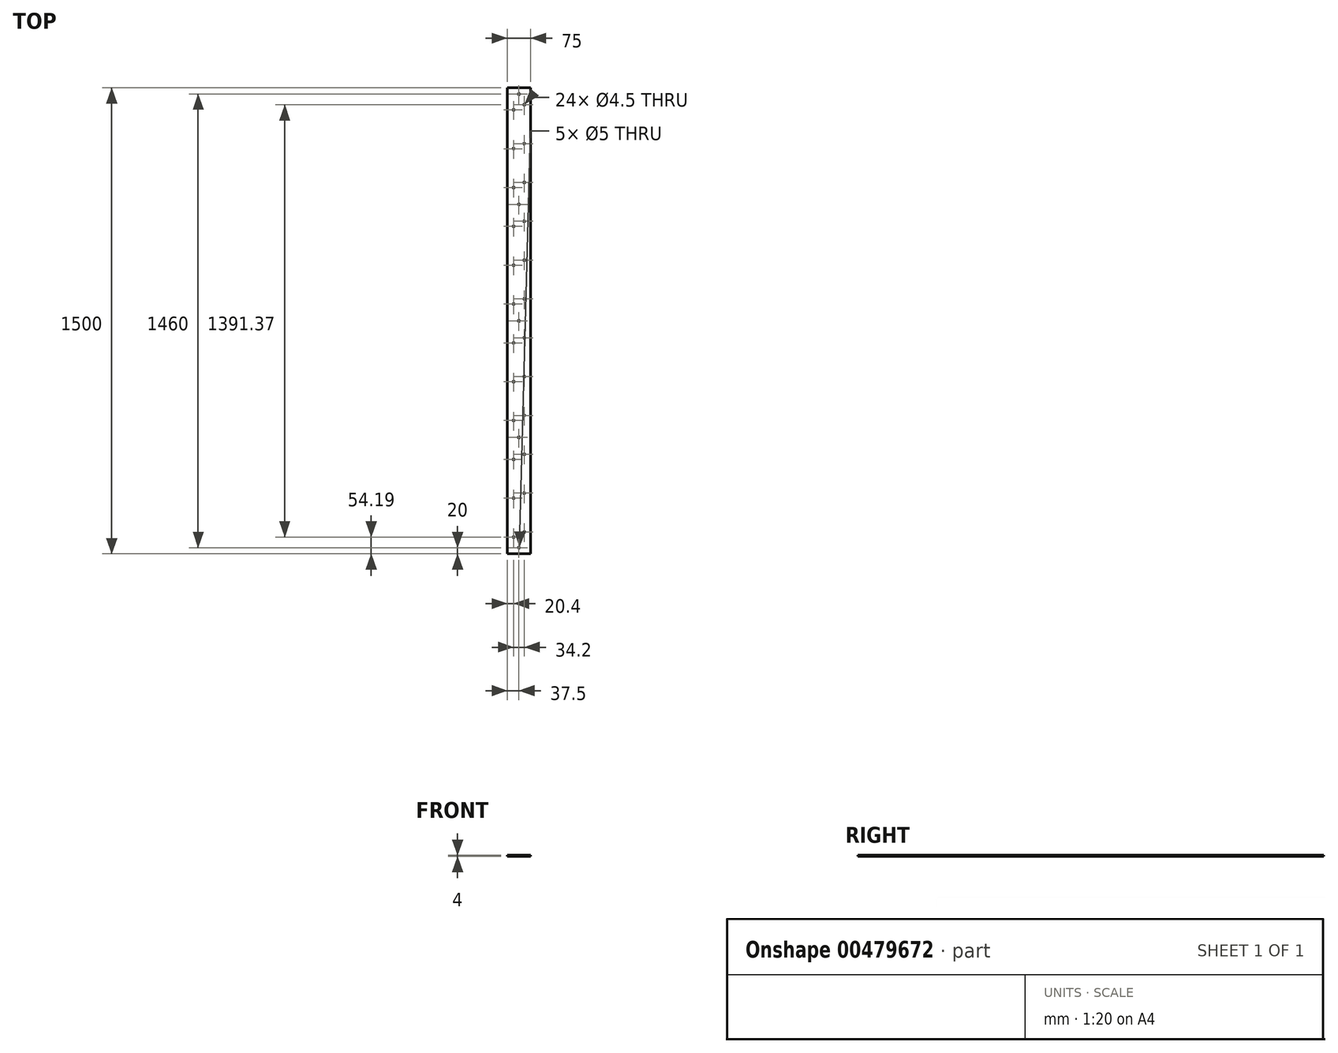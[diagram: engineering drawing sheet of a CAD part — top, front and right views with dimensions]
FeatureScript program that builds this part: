
annotation { "Feature Type Name" : "Feature", "Feature Type Description" : "" }
export const myFeature = defineFeature(function(context is Context, id is Id, definition is map)
    precondition{}
    {
        {
            var Q0;
            Q0=qCreatedBy(makeId("Top.planeOp"),FACE);
            var sketch = newSketch(context, id + "F0", { "sketchPlane" : qUnion([Q0])});
            skLineSegment(sketch, "E0.bottom", {"start": v(37.5, -750) * mm, "end": v(-37.5, -750) * mm});
            skLineSegment(sketch, "E0.top", {"start": v(37.5, 750) * mm, "end": v(-37.5, 750) * mm});
            skLineSegment(sketch, "E0.left", {"start": v(37.5, -750) * mm, "end": v(37.5, 750) * mm});
            skLineSegment(sketch, "E0.right", {"start": v(-37.5, -750) * mm, "end": v(-37.5, 750) * mm});
            skPoint(sketch, "E0.middle", {"position": v(0, 0) * mm});
            skCircle(sketch, "E1", {"center": v(-17.1, -695.81) * mm, "radius": 2.25 * mm});
            skCircle(sketch, "E2", {"center": v(17.1, -679.44) * mm, "radius": 2.25 * mm});
            skCircle(sketch, "E3.0.1.0", {"center": v(-17.1, -570.81) * mm, "radius": 2.25 * mm});
            skCircle(sketch, "E3.0.1.1", {"center": v(17.1, -554.44) * mm, "radius": 2.25 * mm});
            skCircle(sketch, "E3.0.2.0", {"center": v(-17.1, -445.81) * mm, "radius": 2.25 * mm});
            skCircle(sketch, "E3.0.2.1", {"center": v(17.1, -429.44) * mm, "radius": 2.25 * mm});
            skCircle(sketch, "E3.0.3.0", {"center": v(-17.1, -320.81) * mm, "radius": 2.25 * mm});
            skCircle(sketch, "E3.0.3.1", {"center": v(17.1, -304.44) * mm, "radius": 2.25 * mm});
            skCircle(sketch, "E3.0.4.0", {"center": v(-17.1, -195.81) * mm, "radius": 2.25 * mm});
            skCircle(sketch, "E3.0.4.1", {"center": v(17.1, -179.44) * mm, "radius": 2.25 * mm});
            skCircle(sketch, "E3.0.5.0", {"center": v(-17.1, -70.81) * mm, "radius": 2.25 * mm});
            skCircle(sketch, "E3.0.5.1", {"center": v(17.1, -54.44) * mm, "radius": 2.25 * mm});
            skCircle(sketch, "E3.0.6.0", {"center": v(-17.1, 54.19) * mm, "radius": 2.25 * mm});
            skCircle(sketch, "E3.0.6.1", {"center": v(17.1, 70.56) * mm, "radius": 2.25 * mm});
            skCircle(sketch, "E3.0.7.0", {"center": v(-17.1, 179.19) * mm, "radius": 2.25 * mm});
            skCircle(sketch, "E3.0.7.1", {"center": v(17.1, 195.56) * mm, "radius": 2.25 * mm});
            skCircle(sketch, "E3.0.8.0", {"center": v(-17.1, 304.19) * mm, "radius": 2.25 * mm});
            skCircle(sketch, "E3.0.8.1", {"center": v(17.1, 320.56) * mm, "radius": 2.25 * mm});
            skCircle(sketch, "E3.0.9.0", {"center": v(-17.1, 429.19) * mm, "radius": 2.25 * mm});
            skCircle(sketch, "E3.0.9.1", {"center": v(17.1, 445.56) * mm, "radius": 2.25 * mm});
            skCircle(sketch, "E3.0.10.0", {"center": v(-17.1, 554.19) * mm, "radius": 2.25 * mm});
            skCircle(sketch, "E3.0.10.1", {"center": v(17.1, 570.56) * mm, "radius": 2.25 * mm});
            skCircle(sketch, "E3.0.11.0", {"center": v(-17.1, 679.19) * mm, "radius": 2.25 * mm});
            skCircle(sketch, "E3.0.11.1", {"center": v(17.1, 695.56) * mm, "radius": 2.25 * mm});
            skLineSegment(sketch, "E3.direction1", {"start": v(-17.1, -695.81) * mm, "end": v(1.36, -695.81) * mm, "construction": true});
            skLineSegment(sketch, "E3.direction2", {"start": v(-17.1, -695.81) * mm, "end": v(-17.1, -570.81) * mm, "construction": true});
            skPoint(sketch, "E4", {"position": v(0, 730) * mm});
            skPoint(sketch, "E4.positionSnap0", {"position": v(0, 750) * mm});
            skPoint(sketch, "E5", {"position": v(0, 375) * mm});
            skPoint(sketch, "E6", {"position": v(0, -730) * mm});
            skPoint(sketch, "E6.positionSnap0", {"position": v(0, -750) * mm});
            skPoint(sketch, "E7", {"position": v(0, -375) * mm});
            skSolve(sketch);
        }
        {
            var Q0;
            Q0 = qSketchRegion(id + "F0", true);
            extrude(context, id + "F1", {"entities" : qUnion([Q0]), "depth" : 4 * mm, "offsetDistance" : 25 * mm});
        }
        {
            var Q0;
            Q0=sQuery(id+"F0.wireOp",VERTEX,"E4");
            var Q1;
            Q1=sQuery(id+"F0.wireOp",VERTEX,"E5");
            var Q2;
            Q2=sQuery(id+"F0.wireOp",VERTEX,"E0.middle");
            var Q3;
            Q3=sQuery(id+"F0.wireOp",VERTEX,"E7");
            var Q4;
            Q4=sQuery(id+"F0.wireOp",VERTEX,"E6");
            var Q5;
            Q5=makeQuery(id+"F1.opExtrude","SWEPT_BODY",BODY,{"disambiguationData":[OSD([sQuery(id+"F0.wireOp",EDGE,"E0.bottom"),sQuery(id+"F0.wireOp",EDGE,"E0.top"),sQuery(id+"F0.wireOp",EDGE,"E0.left"),sQuery(id+"F0.wireOp",EDGE,"E0.right"),sQuery(id+"F0.wireOp",EDGE,"E1"),sQuery(id+"F0.wireOp",EDGE,"E2"),sQuery(id+"F0.wireOp",EDGE,"E3.0.1.0"),sQuery(id+"F0.wireOp",EDGE,"E3.0.1.1"),sQuery(id+"F0.wireOp",EDGE,"E3.0.2.0"),sQuery(id+"F0.wireOp",EDGE,"E3.0.2.1"),sQuery(id+"F0.wireOp",EDGE,"E3.0.3.0"),sQuery(id+"F0.wireOp",EDGE,"E3.0.3.1"),sQuery(id+"F0.wireOp",EDGE,"E3.0.4.0"),sQuery(id+"F0.wireOp",EDGE,"E3.0.4.1"),sQuery(id+"F0.wireOp",EDGE,"E3.0.5.0"),sQuery(id+"F0.wireOp",EDGE,"E3.0.5.1"),sQuery(id+"F0.wireOp",EDGE,"E3.0.6.0"),sQuery(id+"F0.wireOp",EDGE,"E3.0.6.1"),sQuery(id+"F0.wireOp",EDGE,"E3.0.7.0"),sQuery(id+"F0.wireOp",EDGE,"E3.0.7.1"),sQuery(id+"F0.wireOp",EDGE,"E3.0.8.0"),sQuery(id+"F0.wireOp",EDGE,"E3.0.8.1"),sQuery(id+"F0.wireOp",EDGE,"E3.0.9.0"),sQuery(id+"F0.wireOp",EDGE,"E3.0.9.1"),sQuery(id+"F0.wireOp",EDGE,"E3.0.10.0"),sQuery(id+"F0.wireOp",EDGE,"E3.0.10.1"),sQuery(id+"F0.wireOp",EDGE,"E3.0.11.0"),sQuery(id+"F0.wireOp",EDGE,"E3.0.11.1")])]});
            hole(context, id + "F2", {"style" : HoleStyle.SIMPLE, "endStyle" : HoleEndStyle.THROUGH, "oppositeDirection" : true, "holeDiameter" : 5 * mm, "majorDiameter" : 5 * mm, "isTappedThrough" : true, "tappedDepth" : 12 * mm, "tapClearance" : 3, "locations" : qUnion([Q0, Q1, Q2, Q3, Q4]), "scope" : qUnion([Q5])});
        }
    });
